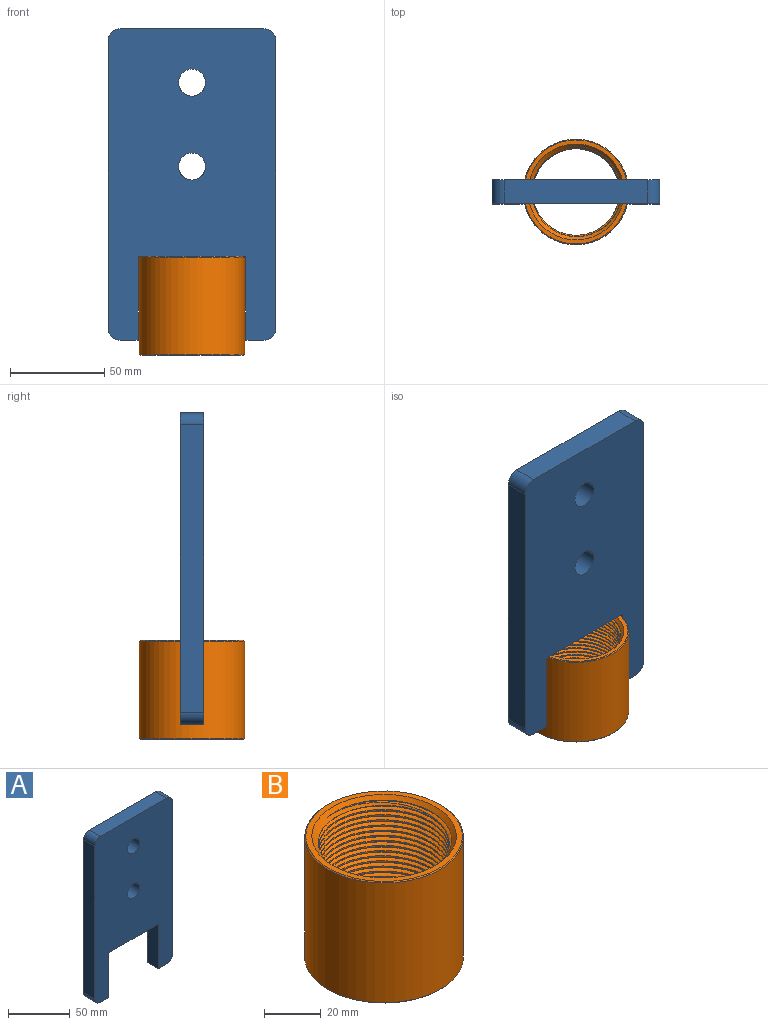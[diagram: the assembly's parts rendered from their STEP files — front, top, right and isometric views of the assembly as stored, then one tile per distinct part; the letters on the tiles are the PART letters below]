
ASSEMBLY  parts=2 mates=1
PART A: 16 faces, bbox 88.9x12.7x165.1 mm
  f0: plane 152.4x12.7mm, normal (1,0,0), area 1935.5mm2, adj f8,f9,f12,f15
  f1: plane 76.2x12.7mm, normal (0,0,1), area 967.7mm2, adj f8,f9,f12,f13
  f2: plane 152.4x12.7mm, normal (-1,0,0), area 1935.5mm2, adj f8,f9,f13,f14
  f3: plane 12.7x9.53mm, normal (0,0,-1), area 121mm2, adj f4,f8,f9,f14
  f4: plane 44.45x12.7mm, normal (1,0,0), area 564.5mm2, adj f3,f5,f8,f9
  f5: plane 57.15x12.7mm, normal (0,0,-1), area 725.8mm2, adj f4,f6,f8,f9
  f6: plane 44.45x12.7mm, normal (-1,0,0), area 564.5mm2, adj f5,f7,f8,f9
  f7: plane 12.7x9.53mm, normal (0,0,-1), area 121mm2, adj f6,f8,f9,f15
  f8: plane 165.1x88.9mm, normal (0,-1,0), area 11781.8mm2, adj f0,f1,f2,f3,f4,f5,f6,f7
  f9: plane 165.1x88.9mm, normal (0,1,0), area 11781.8mm2, adj f0,f1,f2,f3,f4,f5,f6,f7
  f10: cylinder r=7.14mm len=14.29mm, axis (0,1,0), area 570mm2, adj f8,f9
  f11: cylinder r=7.14mm len=14.29mm, axis (0,1,0), area 570mm2, adj f8,f9
  f12: cylinder r=6.35mm len=12.7mm, axis (0,-1,0), area 126.7mm2, adj f0,f1,f8,f9
  f13: cylinder r=6.35mm len=12.7mm, axis (0,1,0), area 126.7mm2, adj f1,f2,f8,f9
  f14: cylinder r=6.35mm len=12.7mm, axis (0,-1,0), area 126.7mm2, adj f2,f3,f8,f9
  f15: cylinder r=6.35mm len=12.7mm, axis (0,1,0), area 126.7mm2, adj f0,f7,f8,f9
PART B: 13 faces, bbox 55.9x55.9x52.4 mm
  f0: cone r=27.54mm half-angle=45deg, axis (0,0,-1), area 97.8mm2, adj f6,f12
  f1: cone r=27.94mm half-angle=45deg, axis (0,0,1), area 97.8mm2, adj f6,f11
  f2: cone r=25.4mm half-angle=40deg, axis (0,0,-1), area 453.9mm2, adj f3,f7,f8,f9,f10,f11
  f3: cone r=25.4mm half-angle=40deg, axis (0,0,-1), area 8.3mm2, adj f2,f7,f10
  f4: cone r=25.4mm half-angle=40deg, axis (0,0,1), area 461.5mm2, adj f5,f7,f8,f9,f10,f12
  f5: cone r=25.4mm half-angle=40deg, axis (0,0,1), area 1.2mm2, adj f4,f7,f9
  f6: cylinder r=27.94mm len=55.88mm, axis (0,0,-1), area 9055.2mm2, adj f0,f1
  f7: cylinder r=22.93mm len=46.5mm, axis (0,0,1), area 1675.1mm2, adj f2,f3,f4,f5,f9,f10
  f8: cylinder r=24.13mm len=49.35mm, axis (0,0,1), area 935.3mm2, adj f2,f4,f9,f10
  f9: bspline ~50.04x48.26mm, area 4430.1mm2, adj f2,f4,f5,f7,f8
  f10: bspline ~50.04x48.24mm, area 4429.6mm2, adj f2,f3,f4,f7,f8
  f11: plane 55.09x55.09mm, normal (0,0,-1), area 356.5mm2, adj f1,f2
  f12: plane 55.09x55.09mm, normal (0,0,1), area 356.5mm2, adj f0,f4
PLACE A t=(0,6.35,64.29)mm
PLACE B at identity
MATE fastened A.f5 <-> B.f0  axis (0,0,-1) through (0,0,26.19)mm
